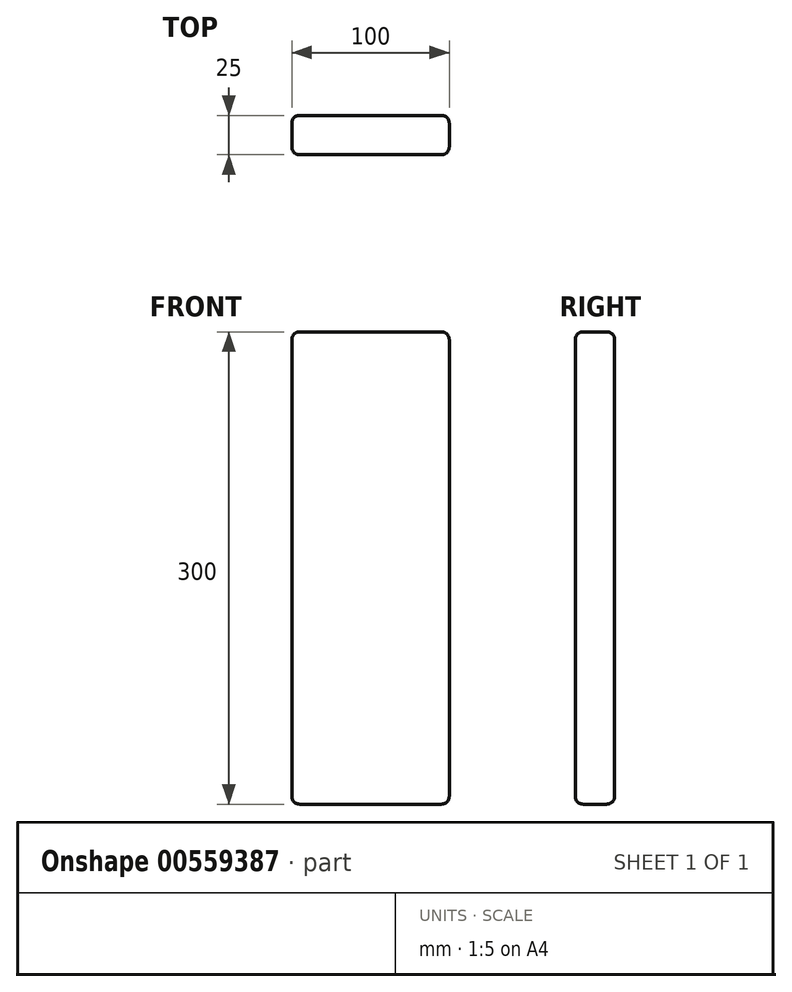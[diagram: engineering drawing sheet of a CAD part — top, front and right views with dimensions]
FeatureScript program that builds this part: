
annotation { "Feature Type Name" : "Feature", "Feature Type Description" : "" }
export const myFeature = defineFeature(function(context is Context, id is Id, definition is map)
    precondition{}
    {
        {
            var Q0;
            Q0=qCreatedBy(makeId("Front.planeOp"),FACE);
            var sketch = newSketch(context, id + "F0", { "sketchPlane" : qUnion([Q0])});
            skLineSegment(sketch, "E0.bottom", {"start": v(0, 0) * mm, "end": v(100, 0) * mm});
            skLineSegment(sketch, "E0.top", {"start": v(0, -300) * mm, "end": v(100, -300) * mm});
            skLineSegment(sketch, "E0.left", {"start": v(0, 0) * mm, "end": v(0, -300) * mm});
            skLineSegment(sketch, "E0.right", {"start": v(100, 0) * mm, "end": v(100, -300) * mm});
            skSolve(sketch);
        }
        {
            var Q0;
            Q0=makeQuery(id+"F0.imprint","IMPRINT",FACE,{"disambiguationData":[TD([[makeQuery(id+"F0.imprint","IMPRINT",EDGE,{"derivedFrom":sQuery(id+"F0.wireOp",EDGE,"E0.bottom")}),-1.0]])]});
            extrude(context, id + "F1", {"entities" : qUnion([Q0]), "depth" : 25 * mm, "offsetDistance" : 25 * mm});
        }
        {
            var Q0;
            Q0=makeQuery(id+"F1.opExtrude","CAP_EDGE",EDGE,{"disambiguationData":[OSD([sQuery(id+"F0.wireOp",EDGE,"E0.left")])],"isStart":false});
            var Q1;
            Q1=makeQuery(id+"F1.opExtrude","SWEPT_EDGE",EDGE,{"disambiguationData":[OSD([sQuery(id+"F0.wireOp",EDGE,"E0.top"),sQuery(id+"F0.wireOp",EDGE,"E0.left")])]});
            var Q2;
            Q2=makeQuery(id+"F1.opExtrude","CAP_EDGE",EDGE,{"disambiguationData":[OSD([sQuery(id+"F0.wireOp",EDGE,"E0.top")])],"isStart":false});
            var Q3;
            Q3=makeQuery(id+"F1.opExtrude","CAP_EDGE",EDGE,{"disambiguationData":[OSD([sQuery(id+"F0.wireOp",EDGE,"E0.top")])],"isStart":true});
            var Q4;
            Q4=makeQuery(id+"F1.opExtrude","CAP_EDGE",EDGE,{"disambiguationData":[OSD([sQuery(id+"F0.wireOp",EDGE,"E0.left")])],"isStart":true});
            var Q5;
            Q5=makeQuery(id+"F1.opExtrude","SWEPT_EDGE",EDGE,{"disambiguationData":[OSD([sQuery(id+"F0.wireOp",EDGE,"E0.top"),sQuery(id+"F0.wireOp",EDGE,"E0.right")])]});
            var Q6;
            Q6=makeQuery(id+"F1.opExtrude","CAP_EDGE",EDGE,{"disambiguationData":[OSD([sQuery(id+"F0.wireOp",EDGE,"E0.right")])],"isStart":false});
            var Q7;
            Q7=makeQuery(id+"F1.opExtrude","CAP_EDGE",EDGE,{"disambiguationData":[OSD([sQuery(id+"F0.wireOp",EDGE,"E0.bottom")])],"isStart":false});
            var Q8;
            Q8=makeQuery(id+"F1.opExtrude","CAP_EDGE",EDGE,{"disambiguationData":[OSD([sQuery(id+"F0.wireOp",EDGE,"E0.bottom")])],"isStart":true});
            var Q9;
            Q9=makeQuery(id+"F1.opExtrude","CAP_FACE",FACE,{"disambiguationData":[OSD([sQuery(id+"F0.wireOp",EDGE,"E0.bottom"),sQuery(id+"F0.wireOp",EDGE,"E0.top"),sQuery(id+"F0.wireOp",EDGE,"E0.left"),sQuery(id+"F0.wireOp",EDGE,"E0.right")])],"isStart":true});
            var Q10;
            Q10=makeQuery(id+"F1.opExtrude","SWEPT_EDGE",EDGE,{"disambiguationData":[OSD([sQuery(id+"F0.wireOp",EDGE,"E0.bottom"),sQuery(id+"F0.wireOp",EDGE,"E0.right")])]});
            var Q11;
            Q11=makeQuery(id+"F1.opExtrude","SWEPT_EDGE",EDGE,{"disambiguationData":[OSD([sQuery(id+"F0.wireOp",EDGE,"E0.bottom"),sQuery(id+"F0.wireOp",EDGE,"E0.left")])]});
            fillet(context, id + "F2", {"entities" : qUnion([Q0, Q1, Q2, Q3, Q4, Q5, Q6, Q7, Q8, Q9, Q10, Q11]), "radius" : 5 * mm, "tangentPropagation" : true, "allowEdgeOverflow" : false});
        }
    });
